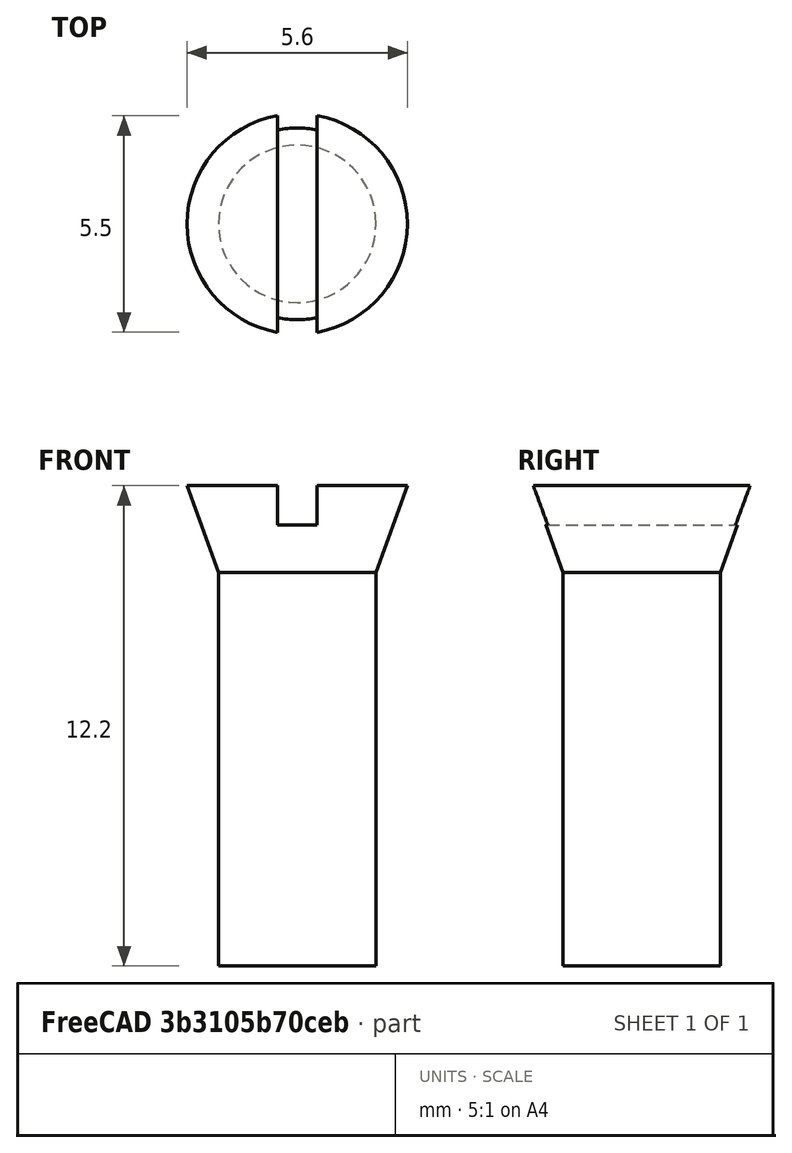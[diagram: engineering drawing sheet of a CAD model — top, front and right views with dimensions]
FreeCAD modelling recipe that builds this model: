
FCSTD DOCUMENT  (FreeCAD 0.21R33694 (Git))
Label: OJT1_T14R01.vis
License: All rights reserved
LicenseURL: http://en.wikipedia.org/wiki/All_rights_reserved
objects: Part::Cone×1, Part::Box×1, Part::Cut×1, Part::Cylinder×1, Part::Fuse×1
note: 5 computed .brp shape members not serialized (recipe doc carries the construction recipe); baked Part::Feature solids carry a one-line shape summary decoded from their .brp

FEATURE [Part::Cone] Cone  label="Con"
  Angle = 360
  AttacherType = Attacher::AttachEngine3D
  Height = 2.2
  Radius1 = 2
  Radius2 = 2.8
FEATURE [Part::Box] Box  label="Cub"
  AttacherType = Attacher::AttachEngine3D
  Height = 10
  Length = 1
  Placement = pos=(-0.5,-4,1.2) rot=(0,0,1;0rad)
  Width = 10
FEATURE [Part::Cut] Cut
  Base = -> Cone
  Placement = pos=(0,0,10) rot=(0,0,1;0rad)
  Refine = true
  Tool = -> Box
FEATURE [Part::Cylinder] Cylinder  label="Cilindre"
  Angle = 360
  AttacherType = Attacher::AttachEngine3D
  FirstAngle = 0
  Height = 10
  Radius = 2
  SecondAngle = 0
FEATURE [Part::Fuse] Fusion
  Base = -> Cut
  Refine = true
  Tool = -> Cylinder
